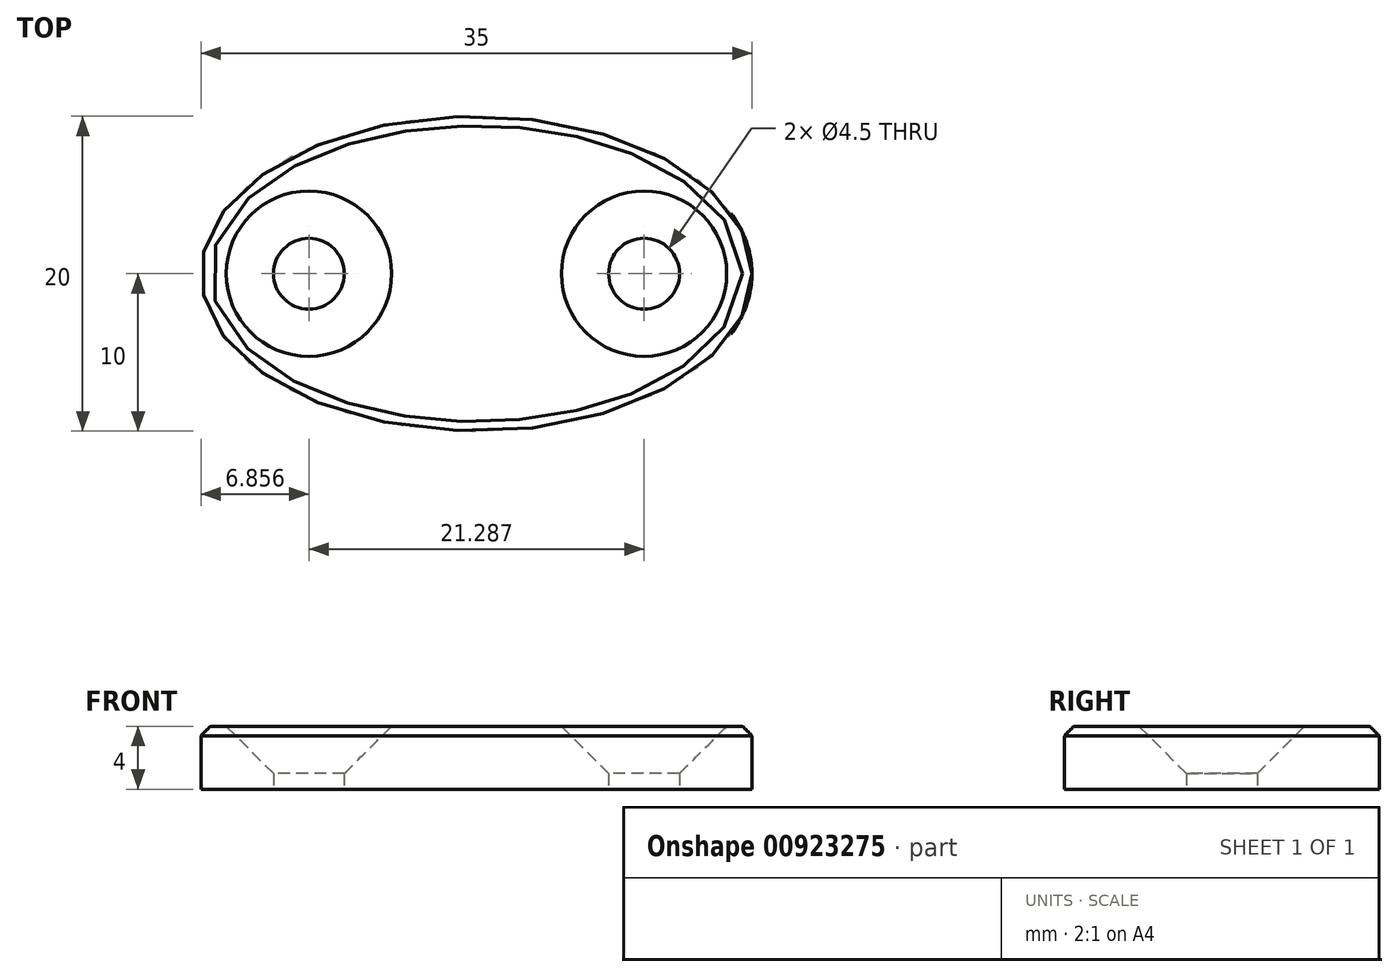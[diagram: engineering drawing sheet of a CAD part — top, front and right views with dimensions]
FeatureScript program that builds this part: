
annotation { "Feature Type Name" : "Feature", "Feature Type Description" : "" }
export const myFeature = defineFeature(function(context is Context, id is Id, definition is map)
    precondition{}
    {
        {
            var Q0;
            Q0=qCreatedBy(makeId("Top.planeOp"),FACE);
            var sketch = newSketch(context, id + "F0", { "sketchPlane" : qUnion([Q0])});
            skEllipse(sketch, "E0", {"center": v(0, 0) * mm, "majorRadius": 17.5 * mm, "minorRadius": 10 * mm, "majorAxis": v(1, 0)});
            skLineSegment(sketch, "E1", {"start": v(-10.64, 0) * mm, "end": v(10.64, 0) * mm, "construction": true});
            skPoint(sketch, "E1.startSnap0", {"position": v(-17.5, 0) * mm});
            skLineSegment(sketch, "E2", {"start": v(0, 0) * mm, "end": v(0, 10) * mm, "construction": true});
            skCircle(sketch, "E3", {"center": v(-10.64, 0) * mm, "radius": 2.25 * mm});
            skCircle(sketch, "E4", {"center": v(10.64, 0) * mm, "radius": 2.25 * mm});
            skSolve(sketch);
        }
        {
            var Q0;
            Q0=makeQuery(id+"F0.imprint","IMPRINT",FACE,{"disambiguationData":[TD([[makeQuery(id+"F0.imprint","IMPRINT",EDGE,{"derivedFrom":sQuery(id+"F0.wireOp",EDGE,"E0")}),1.0]])]});
            extrude(context, id + "F1", {"entities" : qUnion([Q0]), "depth" : 4 * mm, "offsetDistance" : 25 * mm});
        }
        {
            var Q0;
            Q0=makeQuery(id+"F1.opExtrude","CAP_EDGE",EDGE,{"disambiguationData":[OSD([sQuery(id+"F0.wireOp",EDGE,"E3")])],"isStart":false});
            var Q1;
            Q1=makeQuery(id+"F1.opExtrude","CAP_EDGE",EDGE,{"disambiguationData":[OSD([sQuery(id+"F0.wireOp",EDGE,"E4")])],"isStart":false});
            chamfer(context, id + "F2", {"entities" : qUnion([Q0, Q1]), "width" : 3 * mm, "tangentPropagation" : true});
        }
        {
            var Q0;
            Q0=makeQuery(id+"F1.opExtrude","CAP_EDGE",EDGE,{"disambiguationData":[OSD([sQuery(id+"F0.wireOp",EDGE,"E0")])],"isStart":false});
            chamfer(context, id + "F3", {"entities" : qUnion([Q0]), "width" : .6 * mm, "tangentPropagation" : true});
        }
    });
